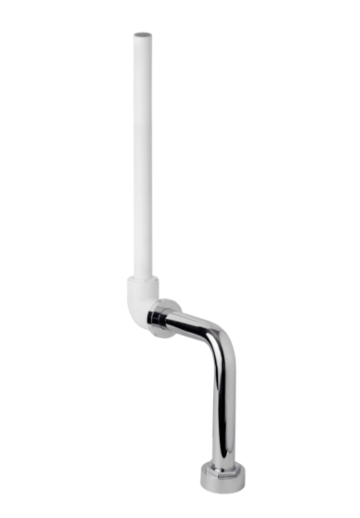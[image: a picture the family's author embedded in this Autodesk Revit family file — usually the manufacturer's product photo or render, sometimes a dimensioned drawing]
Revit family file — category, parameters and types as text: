
# Revit family: IS-CO02-211 CONEXION SUPERIOR SANITARIO
name_source: partatom
category: Aparatos sanitarios
revit_build: Autodesk Revit 2018 (Build: 20170223_1515(x64)
units: mm (PartAtom-declared; Revit-internal decimal feet)

## family parameters
Anfitrión = Cara
Compartido = No
Corte con vacíos al cargar = No
Cota de conector redondo = Diámetro de uso
Número OmniClass = 23.31.11.00
Punto de cálculo de habitación = No
Tipo de pieza = Normal

## types (1)
- IS-CO02-211
    Alto = 1120 mm  [stored 3.67454 ft]
    Ancho = 189.8 mm
    Base = 75 mm
    Codo = 68.5 mm
    Conexión AC = Sí
    Conexión AF = Sí
    Conexión de residuos = No
    Conexión de ventilación = No
    Descripción = Conexion
    Elevación por defecto = 0 mm  [stored 0 ft]
    Fabricante = Gricol
    Imagen de tipo = CONEXION SUPERIOR SANITARIO.png
    Link Ficha Tecnica = http://infotecnica.gricol.com
    Modelo = IS-CO02-211
    PVC Blanco = PVC Blanco
    Plastico ABS Cromado = Plastico - ABS Cromado
    Product Name = CONEXION SUPERIOR SANITARIO
    Tuerca = 75 mm
    URL = https://www.gricol.com

note: [stored X ft] marks values corroborated as IEEE doubles in the binary element streams (Revit-internal decimal feet)

## geometry (parser evidence)
native form markers: Blend x2, Sweep x4
no freeform markers — native parametric forms only
